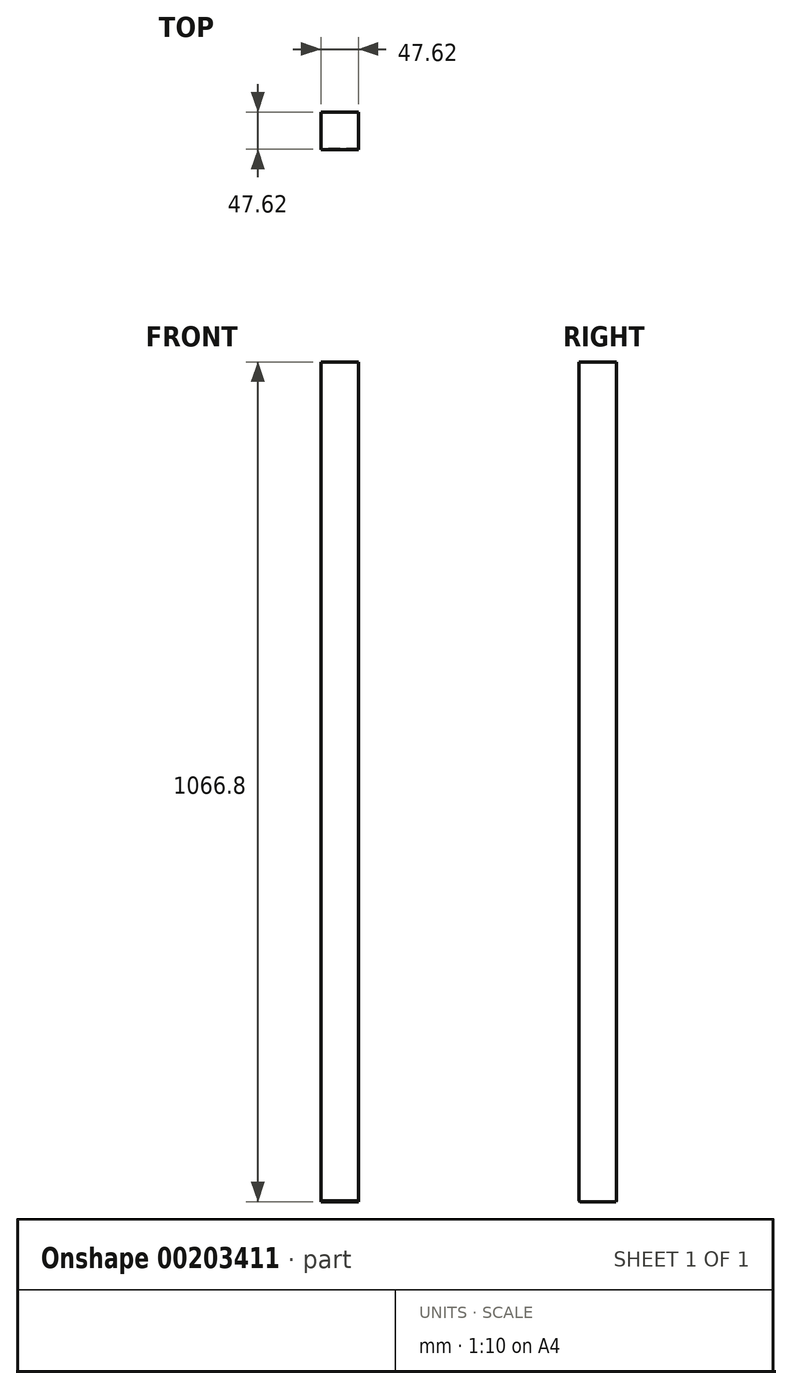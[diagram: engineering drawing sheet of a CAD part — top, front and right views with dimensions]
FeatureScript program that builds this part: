
annotation { "Feature Type Name" : "Feature", "Feature Type Description" : "" }
export const myFeature = defineFeature(function(context is Context, id is Id, definition is map)
    precondition{}
    {
        {
            var Q0;
            Q0=qCreatedBy(makeId("Top.planeOp"),FACE);
            var sketch = newSketch(context, id + "F0", { "sketchPlane" : qUnion([Q0])});
            skLineSegment(sketch, "E0.bottom", {"start": v(23.81, -23.81) * mm, "end": v(-23.81, -23.81) * mm});
            skLineSegment(sketch, "E0.top", {"start": v(23.81, 23.81) * mm, "end": v(-23.81, 23.81) * mm});
            skLineSegment(sketch, "E0.left", {"start": v(23.81, -23.81) * mm, "end": v(23.81, 23.81) * mm});
            skLineSegment(sketch, "E0.right", {"start": v(-23.81, -23.81) * mm, "end": v(-23.81, 23.81) * mm});
            skPoint(sketch, "E0.middle", {"position": v(0, 0) * mm});
            skSolve(sketch);
        }
        {
            var Q0;
            Q0 = qSketchRegion(id + "F0", true);
            extrude(context, id + "F1", {"entities" : qUnion([Q0]), "depth" : 1066.8 * mm});
        }
        {
            var Q0;
            Q0=makeQuery(id+"F1.opExtrude","CAP_EDGE",EDGE,{"disambiguationData":[OSD([sQuery(id+"F0.wireOp",EDGE,"E0.bottom")])],"isStart":true});
            var Q1;
            Q1=makeQuery(id+"F1.opExtrude","CAP_EDGE",EDGE,{"disambiguationData":[OSD([sQuery(id+"F0.wireOp",EDGE,"E0.top")])],"isStart":true});
            chamfer(context, id + "F2", {"entities" : qUnion([Q0, Q1]), "width" : ((1 + (5 / 8)) / 2) * mm, "tangentPropagation" : true});
        }
    });
